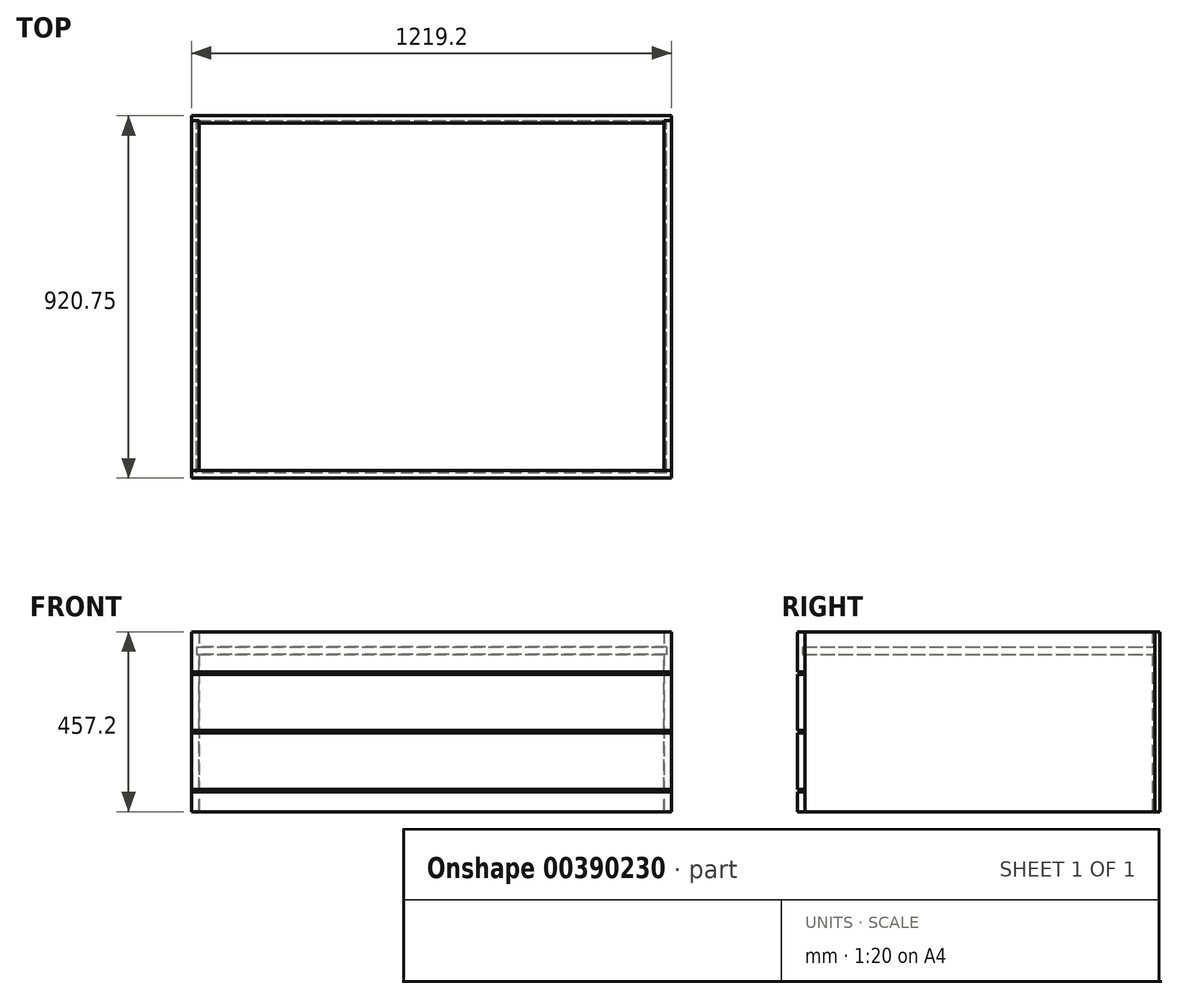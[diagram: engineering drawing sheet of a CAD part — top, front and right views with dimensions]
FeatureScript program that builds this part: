
annotation { "Feature Type Name" : "Feature", "Feature Type Description" : "" }
export const myFeature = defineFeature(function(context is Context, id is Id, definition is map)
    precondition{}
    {
        {
            var Q0;
            Q0=qCreatedBy(makeId("Front.planeOp"),FACE);
            var sketch = newSketch(context, id + "F0", { "sketchPlane" : qUnion([Q0])});
            skLineSegment(sketch, "E0.bottom", {"start": v(609.6, 228.6) * mm, "end": v(-609.6, 228.6) * mm});
            skLineSegment(sketch, "E0.top", {"start": v(609.6, -228.6) * mm, "end": v(-609.6, -228.6) * mm});
            skLineSegment(sketch, "E0.left", {"start": v(609.6, 228.6) * mm, "end": v(609.6, -228.6) * mm});
            skLineSegment(sketch, "E0.right", {"start": v(-609.6, 228.6) * mm, "end": v(-609.6, -228.6) * mm});
            skPoint(sketch, "E0.middle", {"position": v(0, 0) * mm});
            skSolve(sketch);
        }
        {
            var Q0;
            Q0=makeQuery(id+"F0.imprint","IMPRINT",FACE,{"disambiguationData":[TD([[makeQuery(id+"F0.imprint","IMPRINT",EDGE,{"derivedFrom":sQuery(id+"F0.wireOp",EDGE,"E0.bottom")}),1.0]])]});
            extrude(context, id + "F1", {"entities" : qUnion([Q0]), "oppositeDirection" : true, "depth" : 19.05 * mm});
        }
        {
            var Q0;
            Q0=makeQuery(id+"F1.opExtrude","CAP_FACE",FACE,{"disambiguationData":[OSD([sQuery(id+"F0.wireOp",EDGE,"E0.bottom"),sQuery(id+"F0.wireOp",EDGE,"E0.top"),sQuery(id+"F0.wireOp",EDGE,"E0.left"),sQuery(id+"F0.wireOp",EDGE,"E0.right")])],"isStart":true});
            var sketch = newSketch(context, id + "F2", { "sketchPlane" : qUnion([Q0])});
            skLineSegment(sketch, "E1.bottom", {"start": v(-609.6, 228.6) * mm, "end": v(-590.55, 228.6) * mm});
            skLineSegment(sketch, "E1.top", {"start": v(-609.6, -228.6) * mm, "end": v(-590.55, -228.6) * mm});
            skLineSegment(sketch, "E1.left", {"start": v(-609.6, 228.6) * mm, "end": v(-609.6, -228.6) * mm});
            skLineSegment(sketch, "E1.right", {"start": v(-590.55, 228.6) * mm, "end": v(-590.55, 190.5) * mm});
            skLineSegment(sketch, "E2.bottom", {"start": v(609.6, 228.6) * mm, "end": v(590.55, 228.6) * mm});
            skLineSegment(sketch, "E2.top", {"start": v(609.6, -228.6) * mm, "end": v(590.55, -228.6) * mm});
            skLineSegment(sketch, "E2.left", {"start": v(609.6, 228.6) * mm, "end": v(609.6, -228.6) * mm});
            skLineSegment(sketch, "E2.right", {"start": v(590.55, 228.6) * mm, "end": v(590.55, 190.5) * mm});
            skLineSegment(sketch, "E3.bottom", {"start": v(-590.55, 190.5) * mm, "end": v(590.55, 190.5) * mm});
            skLineSegment(sketch, "E3.top", {"start": v(-590.55, 171.45) * mm, "end": v(590.55, 171.45) * mm});
            skLineSegment(sketch, "E3.left", {"start": v(-609.6, 190.5) * mm, "end": v(-609.6, 171.45) * mm});
            skLineSegment(sketch, "E3.right", {"start": v(609.6, 190.5) * mm, "end": v(609.6, 171.45) * mm});
            skLineSegment(sketch, "E4.trimOffspring", {"start": v(-590.55, 171.45) * mm, "end": v(-590.55, -228.6) * mm});
            skLineSegment(sketch, "E5.trimOffspring", {"start": v(590.55, 171.45) * mm, "end": v(590.55, -228.6) * mm});
            skSolve(sketch);
        }
        {
            var Q0;
            {var subQ4=sQuery(id+"F2.wireOp",EDGE,"E1.bottom");Q0=makeQuery(id+"F2.imprint","IMPRINT",FACE,{"disambiguationData":[TD([[makeQuery(id+"F2.imprint","IMPRINT",EDGE,{"derivedFrom":subQ4}),1.0]])]});}
            extrude(context, id + "F3", {"entities" : qUnion([Q0]), "operationType" : NewBodyOperationType.REMOVE, "oppositeDirection" : true, "depth" : 6.35 * mm});
        }
        {
            var Q0;
            Q0=makeQuery(id+"F1.opExtrude","SWEPT_FACE",FACE,{"disambiguationData":[OSD([sQuery(id+"F0.wireOp",EDGE,"E0.bottom")])]});
            var sketch = newSketch(context, id + "F4", { "sketchPlane" : qUnion([Q0])});
            skLineSegment(sketch, "E6.bottom", {"start": v(-609.6, 6.35) * mm, "end": v(-590.55, 6.35) * mm});
            skLineSegment(sketch, "E6.top", {"start": v(-609.6, -882.65) * mm, "end": v(-590.55, -882.65) * mm});
            skLineSegment(sketch, "E6.left", {"start": v(-609.6, 6.35) * mm, "end": v(-609.6, -882.65) * mm});
            skLineSegment(sketch, "E6.right", {"start": v(-590.55, 6.35) * mm, "end": v(-590.55, -882.65) * mm});
            skSolve(sketch);
        }
        {
            var Q0;
            {var subQ3=sQuery(id+"F4.wireOp",EDGE,"E6.bottom");Q0=makeQuery(id+"F4.imprint","IMPRINT",FACE,{"disambiguationData":[TD([[makeQuery(id+"F4.imprint","IMPRINT",EDGE,{"derivedFrom":subQ3}),1.0]])]});}
            var Q1;
            Q1=makeQuery(id+"F1.opExtrude","SWEPT_FACE",FACE,{"disambiguationData":[OSD([sQuery(id+"F0.wireOp",EDGE,"E0.top")])]});
            extrude(context, id + "F5", {"entities" : qUnion([Q0]), "endBound" : BoundingType.UP_TO_SURFACE, "oppositeDirection" : true, "endBoundEntityFace" : qUnion([Q1]), "depth" : 25.4 * mm});
        }
        {
            var Q0;
            Q0=makeQuery(id+"F5.opExtrude","SWEPT_FACE",FACE,{"disambiguationData":[OSD([sQuery(id+"F4.wireOp",EDGE,"E6.right")])]});
            var sketch = newSketch(context, id + "F6", { "sketchPlane" : qUnion([Q0])});
            skLineSegment(sketch, "E7.bottom", {"start": v(-882.65, 190.5) * mm, "end": v(6.35, 190.5) * mm});
            skLineSegment(sketch, "E7.top", {"start": v(-882.65, 171.45) * mm, "end": v(6.35, 171.45) * mm});
            skLineSegment(sketch, "E7.left", {"start": v(-882.65, 190.5) * mm, "end": v(-882.65, 171.45) * mm});
            skLineSegment(sketch, "E7.right", {"start": v(6.35, 190.5) * mm, "end": v(6.35, 171.45) * mm});
            skSolve(sketch);
        }
        {
            var Q0;
            Q0=makeQuery(id+"F6.imprint","IMPRINT",FACE,{"disambiguationData":[TD([[makeQuery(id+"F6.imprint","IMPRINT",EDGE,{"derivedFrom":sQuery(id+"F6.wireOp",EDGE,"E7.bottom")}),-1.0]])]});
            extrude(context, id + "F7", {"entities" : qUnion([Q0]), "operationType" : NewBodyOperationType.REMOVE, "oppositeDirection" : true, "depth" : 6.35 * mm});
        }
        {
            var Q0;
            Q0=makeQuery(id+"F5.opExtrude","SWEPT_BODY",BODY,{"disambiguationData":[OSD([sQuery(id+"F4.wireOp",EDGE,"E6.bottom"),sQuery(id+"F4.wireOp",EDGE,"E6.top"),sQuery(id+"F4.wireOp",EDGE,"E6.left"),sQuery(id+"F4.wireOp",EDGE,"E6.right")])]});
            var Q1;
            Q1=qCreatedBy(makeId("Right.planeOp"),FACE);
            mirror(context, id + "F8", {"entities" : qUnion([Q0]), "mirrorPlane" : qUnion([Q1])});
        }
        {
            var Q0;
            Q0=makeQuery(id+"F5.opExtrude","SWEPT_FACE",FACE,{"disambiguationData":[OSD([sQuery(id+"F4.wireOp",EDGE,"E6.top")])]});
            var sketch = newSketch(context, id + "F9", { "sketchPlane" : qUnion([Q0])});
            skLineSegment(sketch, "E8.bottom", {"start": v(-609.6, 228.6) * mm, "end": v(609.6, 228.6) * mm});
            skLineSegment(sketch, "E8.top", {"start": v(-609.6, 127) * mm, "end": v(609.6, 127) * mm});
            skLineSegment(sketch, "E8.left", {"start": v(-609.6, 228.6) * mm, "end": v(-609.6, 127) * mm});
            skLineSegment(sketch, "E8.right", {"start": v(609.6, 228.6) * mm, "end": v(609.6, 127) * mm});
            skSolve(sketch);
        }
        {
            var Q0;
            {var subQ4=sQuery(id+"F9.wireOp",EDGE,"E8.right");Q0=makeQuery(id+"F9.imprint","IMPRINT",FACE,{"disambiguationData":[TD([[makeQuery(id+"F9.imprint","IMPRINT",EDGE,{"derivedFrom":subQ4}),-1.0]])]});}
            var Q1;
            {var subQ4=sQuery(id+"F9.wireOp",EDGE,"E8.left");Q1=makeQuery(id+"F9.imprint","IMPRINT",FACE,{"disambiguationData":[TD([[makeQuery(id+"F9.imprint","IMPRINT",EDGE,{"derivedFrom":subQ4}),-1.0]])]});}
            extrude(context, id + "F10", {"entities" : qUnion([Q0, Q1]), "depth" : 19.05 * mm});
        }
        {
            var Q0;
            Q0=makeQuery(id+"F10.opExtrude","CAP_FACE",FACE,{"disambiguationData":[OSD([sQuery(id+"F9.wireOp",EDGE,"E8.bottom"),sQuery(id+"F9.wireOp",EDGE,"E8.top"),sQuery(id+"F9.wireOp",EDGE,"E8.left"),sQuery(id+"F9.wireOp",EDGE,"E8.right")])],"isStart":true});
            var sketch = newSketch(context, id + "F11", { "sketchPlane" : qUnion([Q0])});
            skLineSegment(sketch, "E9.bottom", {"start": v(-596.9, 190.5) * mm, "end": v(596.9, 190.5) * mm});
            skLineSegment(sketch, "E9.top", {"start": v(-596.9, 171.45) * mm, "end": v(596.9, 171.45) * mm});
            skLineSegment(sketch, "E9.left", {"start": v(-596.9, 190.5) * mm, "end": v(-596.9, 171.45) * mm});
            skLineSegment(sketch, "E9.right", {"start": v(596.9, 190.5) * mm, "end": v(596.9, 171.45) * mm});
            skSolve(sketch);
        }
        {
            var Q0;
            Q0=makeQuery(id+"F11.imprint","IMPRINT",FACE,{"disambiguationData":[TD([[makeQuery(id+"F11.imprint","IMPRINT",EDGE,{"derivedFrom":sQuery(id+"F11.wireOp",EDGE,"E9.bottom")}),-1.0]])]});
            extrude(context, id + "F12", {"entities" : qUnion([Q0]), "operationType" : NewBodyOperationType.REMOVE, "oppositeDirection" : true, "depth" : 6.35 * mm});
        }
        {
            var Q0;
            Q0=makeQuery(id+"F5.opExtrude","SWEPT_FACE",FACE,{"disambiguationData":[OSD([sQuery(id+"F4.wireOp",EDGE,"E6.top")])]});
            var sketch = newSketch(context, id + "F13", { "sketchPlane" : qUnion([Q0])});
            skLineSegment(sketch, "E10.bottom", {"start": v(-609.6, -228.6) * mm, "end": v(609.6, -228.6) * mm});
            skLineSegment(sketch, "E10.top", {"start": v(-609.6, -177.8) * mm, "end": v(609.6, -177.8) * mm});
            skLineSegment(sketch, "E10.left", {"start": v(-609.6, -228.6) * mm, "end": v(-609.6, -177.8) * mm});
            skLineSegment(sketch, "E10.right", {"start": v(609.6, -228.6) * mm, "end": v(609.6, -177.8) * mm});
            skSolve(sketch);
        }
        {
            var Q0;
            {var subQ5=sQuery(id+"F13.wireOp",EDGE,"E10.right");Q0=makeQuery(id+"F13.imprint","IMPRINT",FACE,{"disambiguationData":[TD([[makeQuery(id+"F13.imprint","IMPRINT",EDGE,{"derivedFrom":subQ5}),1.0]])]});}
            var Q1;
            {var subQ0=sQuery(id+"F13.wireOp",EDGE,"E10.left");Q1=makeQuery(id+"F13.imprint","IMPRINT",FACE,{"disambiguationData":[TD([[makeQuery(id+"F13.imprint","IMPRINT",EDGE,{"derivedFrom":subQ0}),-1.0]])]});}
            extrude(context, id + "F14", {"entities" : qUnion([Q0, Q1]), "depth" : 19.05 * mm});
        }
        {
            var Q0;
            Q0=makeQuery(id+"F3.boolean.opBoolean","COPY",FACE,{"derivedFrom":makeQuery(id+"F3.opExtrude","CAP_FACE",FACE,{"disambiguationData":[OSD([sQuery(id+"F2.wireOp",EDGE,"E1.bottom"),sQuery(id+"F2.wireOp",EDGE,"E1.top"),sQuery(id+"F2.wireOp",EDGE,"E1.left"),sQuery(id+"F2.wireOp",EDGE,"E1.right"),sQuery(id+"F2.wireOp",EDGE,"E2.bottom"),sQuery(id+"F2.wireOp",EDGE,"E2.top"),sQuery(id+"F2.wireOp",EDGE,"E2.left"),sQuery(id+"F2.wireOp",EDGE,"E2.right"),sQuery(id+"F2.wireOp",EDGE,"E3.bottom"),sQuery(id+"F2.wireOp",EDGE,"E3.top"),sQuery(id+"F2.wireOp",EDGE,"E3.left"),sQuery(id+"F2.wireOp",EDGE,"E3.right"),sQuery(id+"F2.wireOp",EDGE,"E4.trimOffspring"),sQuery(id+"F2.wireOp",EDGE,"E5.trimOffspring")])],"isStart":false})});
            var sketch = newSketch(context, id + "F15", { "sketchPlane" : qUnion([Q0])});
            skLineSegment(sketch, "E11.bottom", {"start": v(-596.9, 190.5) * mm, "end": v(596.9, 190.5) * mm});
            skLineSegment(sketch, "E11.top", {"start": v(-596.9, 171.45) * mm, "end": v(596.9, 171.45) * mm});
            skLineSegment(sketch, "E11.left", {"start": v(-596.9, 190.5) * mm, "end": v(-596.9, 171.45) * mm});
            skLineSegment(sketch, "E11.right", {"start": v(596.9, 190.5) * mm, "end": v(596.9, 171.45) * mm});
            skSolve(sketch);
        }
        {
            var Q0;
            {var subQ2=sQuery(id+"F15.wireOp",EDGE,"E11.left");Q0=makeQuery(id+"F15.imprint","IMPRINT",FACE,{"disambiguationData":[TD([[makeQuery(id+"F15.imprint","IMPRINT",EDGE,{"derivedFrom":subQ2}),1.0]])]});}
            var Q1;
            Q1=makeQuery(id+"F12.boolean.opBoolean","COPY",FACE,{"derivedFrom":makeQuery(id+"F12.opExtrude","CAP_FACE",FACE,{"disambiguationData":[OSD([sQuery(id+"F11.wireOp",EDGE,"E9.bottom"),sQuery(id+"F11.wireOp",EDGE,"E9.top"),sQuery(id+"F11.wireOp",EDGE,"E9.left"),sQuery(id+"F11.wireOp",EDGE,"E9.right")])],"isStart":false})});
            extrude(context, id + "F16", {"entities" : qUnion([Q0]), "endBound" : BoundingType.UP_TO_SURFACE, "endBoundEntityFace" : qUnion([Q1]), "depth" : 25.4 * mm});
        }
        {
            var Q0;
            Q0=makeQuery(id+"F5.opExtrude","SWEPT_FACE",FACE,{"disambiguationData":[OSD([sQuery(id+"F4.wireOp",EDGE,"E6.top")])]});
            var sketch = newSketch(context, id + "F17", { "sketchPlane" : qUnion([Q0])});
            skLineSegment(sketch, "E12.bottom", {"start": v(-609.6, 120.65) * mm, "end": v(609.6, 120.65) * mm});
            skLineSegment(sketch, "E12.top", {"start": v(-609.6, -22.22) * mm, "end": v(609.6, -22.22) * mm});
            skLineSegment(sketch, "E12.left", {"start": v(-609.6, 120.65) * mm, "end": v(-609.6, -22.22) * mm});
            skLineSegment(sketch, "E12.right", {"start": v(609.6, 120.65) * mm, "end": v(609.6, -22.22) * mm});
            skLineSegment(sketch, "E13.bottom", {"start": v(-609.6, -28.57) * mm, "end": v(609.6, -28.57) * mm});
            skLineSegment(sketch, "E13.top", {"start": v(-609.6, -171.45) * mm, "end": v(609.6, -171.45) * mm});
            skLineSegment(sketch, "E13.left", {"start": v(-609.6, -28.57) * mm, "end": v(-609.6, -171.45) * mm});
            skLineSegment(sketch, "E13.right", {"start": v(609.6, -28.57) * mm, "end": v(609.6, -171.45) * mm});
            skSolve(sketch);
        }
        {
            var Q0;
            {var subQ0=sQuery(id+"F17.wireOp",EDGE,"E12.right");Q0=makeQuery(id+"F17.imprint","IMPRINT",FACE,{"disambiguationData":[TD([[makeQuery(id+"F17.imprint","IMPRINT",EDGE,{"derivedFrom":subQ0}),-1.0]])]});}
            var Q1;
            {var subQ0=sQuery(id+"F17.wireOp",EDGE,"E12.left");Q1=makeQuery(id+"F17.imprint","IMPRINT",FACE,{"disambiguationData":[TD([[makeQuery(id+"F17.imprint","IMPRINT",EDGE,{"derivedFrom":subQ0}),-1.0]])]});}
            var Q2;
            {var subQ0=sQuery(id+"F17.wireOp",EDGE,"E13.left");Q2=makeQuery(id+"F17.imprint","IMPRINT",FACE,{"disambiguationData":[TD([[makeQuery(id+"F17.imprint","IMPRINT",EDGE,{"derivedFrom":subQ0}),-1.0]])]});}
            var Q3;
            {var subQ0=sQuery(id+"F17.wireOp",EDGE,"E13.right");Q3=makeQuery(id+"F17.imprint","IMPRINT",FACE,{"disambiguationData":[TD([[makeQuery(id+"F17.imprint","IMPRINT",EDGE,{"derivedFrom":subQ0}),-1.0]])]});}
            extrude(context, id + "F18", {"entities" : qUnion([Q0, Q1, Q2, Q3]), "depth" : 19.05 * mm});
        }
    });
